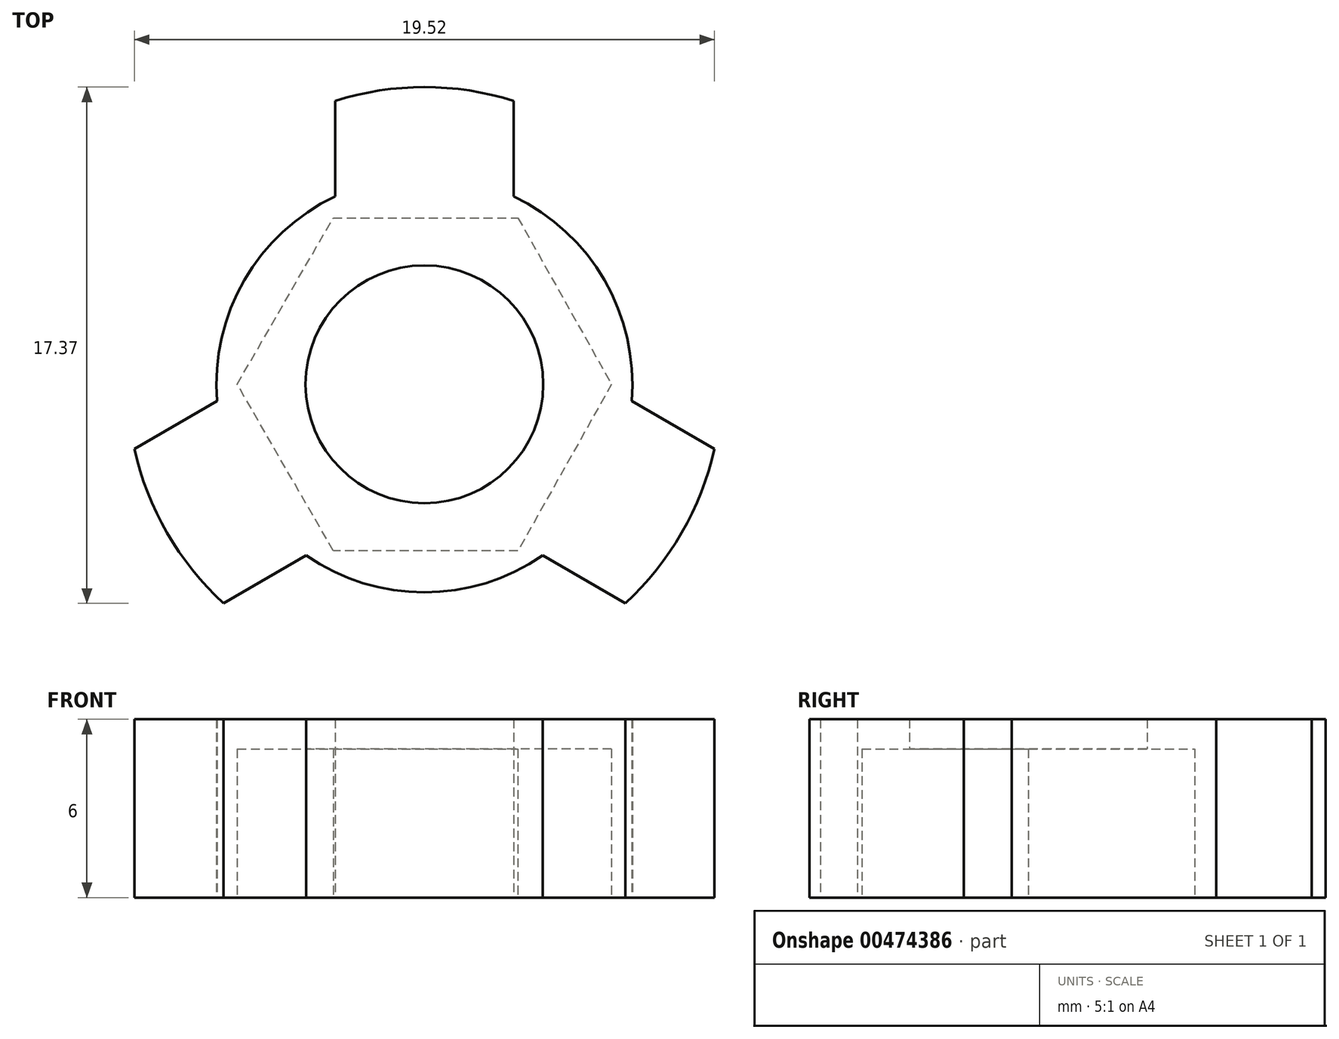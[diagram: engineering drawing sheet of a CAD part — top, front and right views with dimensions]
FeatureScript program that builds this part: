
annotation { "Feature Type Name" : "Feature", "Feature Type Description" : "" }
export const myFeature = defineFeature(function(context is Context, id is Id, definition is map)
    precondition{}
    {
        {
            var Q0;
            Q0=qCreatedBy(makeId("Top.planeOp"),FACE);
            var sketch = newSketch(context, id + "F0", { "sketchPlane" : qUnion([Q0])});
            skArc(sketch, "E0", {"start": v(-9.76, -2.17) * mm, "mid": v(-8.66, -5) * mm, "end": v(-6.76, -7.37) * mm});
            skLineSegment(sketch, "E1", {"start": v(-3, 9.54) * mm, "end": v(-3, 6.32) * mm});
            skLineSegment(sketch, "E2", {"start": v(3, 6.32) * mm, "end": v(3, 9.54) * mm});
            skArc(sketch, "E3.trimOffspring", {"start": v(3, 9.54) * mm, "mid": v(0, 10) * mm, "end": v(-3, 9.54) * mm});
            skArc(sketch, "E4.trimOffspring", {"start": v(6.76, -7.37) * mm, "mid": v(8.66, -5) * mm, "end": v(9.76, -2.17) * mm});
            skLineSegment(sketch, "E5.1.0", {"start": v(-6.76, -7.37) * mm, "end": v(-3.98, -5.76) * mm});
            skLineSegment(sketch, "E5.1.1", {"start": v(-6.98, -0.56) * mm, "end": v(-9.76, -2.17) * mm});
            skLineSegment(sketch, "E5.2.0", {"start": v(9.76, -2.17) * mm, "end": v(6.98, -0.56) * mm});
            skLineSegment(sketch, "E5.2.1", {"start": v(3.98, -5.76) * mm, "end": v(6.76, -7.37) * mm});
            skArc(sketch, "E6", {"start": v(-3, 6.32) * mm, "mid": v(-6.06, 3.5) * mm, "end": v(-6.98, -0.56) * mm});
            skArc(sketch, "E7.trimOffspring", {"start": v(6.98, -0.56) * mm, "mid": v(6.06, 3.5) * mm, "end": v(3, 6.32) * mm});
            skArc(sketch, "E8.trimOffspring", {"start": v(-3.98, -5.76) * mm, "mid": v(0, -7) * mm, "end": v(3.98, -5.76) * mm});
            skCircle(sketch, "E9", {"center": v(0, 0) * mm, "radius": 4 * mm});
            skSolve(sketch);
        }
        {
            var Q0;
            Q0 = qSketchRegion(id + "F0", true);
            extrude(context, id + "F1", {"entities" : qUnion([Q0]), "depth" : 6 * mm});
        }
        {
            var Q0;
            Q0=qCreatedBy(makeId("Top.planeOp"),FACE);
            var sketch = newSketch(context, id + "F2", { "sketchPlane" : qUnion([Q0])});
            skLineSegment(sketch, "E10", {"start": v(0, 0) * mm, "end": v(0, 5.6) * mm, "construction": true});
            skLineSegment(sketch, "E11", {"start": v(0, 5.6) * mm, "end": v(6.3, 5.6) * mm, "construction": true});
            skLineSegment(sketch, "E12", {"start": v(0, 5.6) * mm, "end": v(3.15, 5.6) * mm});
            skLineSegment(sketch, "E13", {"start": v(3.15, 5.6) * mm, "end": v(6.3, 0) * mm});
            skLineSegment(sketch, "E14", {"start": v(6.3, 0) * mm, "end": v(3.15, -5.6) * mm});
            skLineSegment(sketch, "E15", {"start": v(3.15, -5.6) * mm, "end": v(0, -5.6) * mm});
            skLineSegment(sketch, "E16", {"start": v(0, -5.6) * mm, "end": v(-3.07, -5.6) * mm});
            skLineSegment(sketch, "E17", {"start": v(-3.07, -5.6) * mm, "end": v(-6.3, 0) * mm});
            skLineSegment(sketch, "E18", {"start": v(-6.3, 0) * mm, "end": v(-3.07, 5.6) * mm});
            skLineSegment(sketch, "E19", {"start": v(-3.07, 5.6) * mm, "end": v(0, 5.6) * mm});
            skSolve(sketch);
        }
        {
            var Q0;
            Q0 = qSketchRegion(id + "F2", true);
            extrude(context, id + "F3", {"entities" : qUnion([Q0]), "operationType" : NewBodyOperationType.REMOVE, "depth" : 5 * mm});
        }
    });
